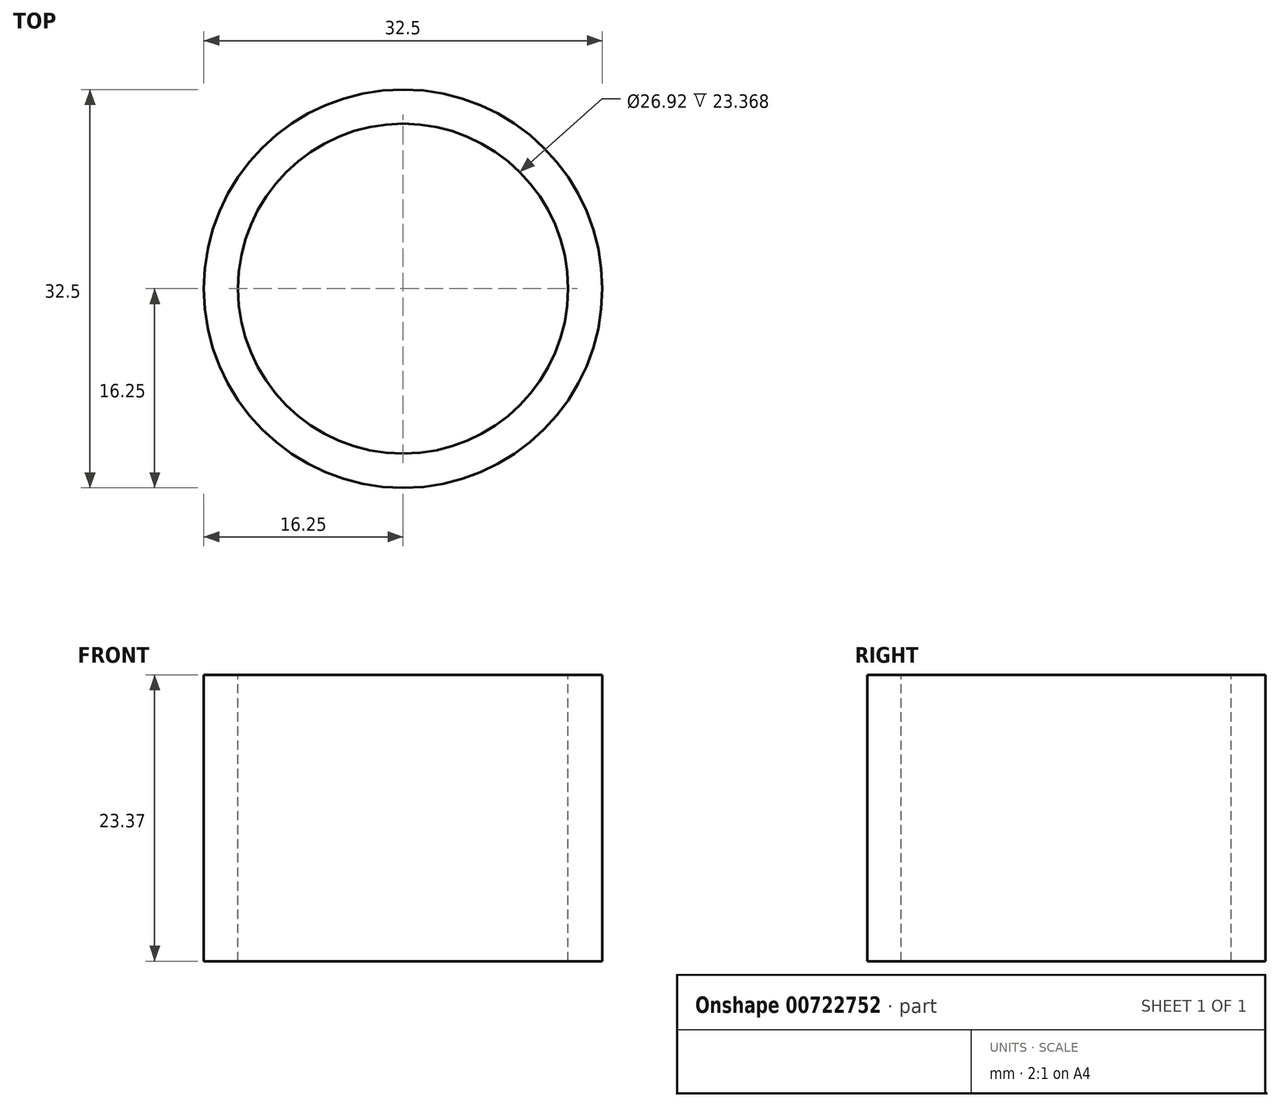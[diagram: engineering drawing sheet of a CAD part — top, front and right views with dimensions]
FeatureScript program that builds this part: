
annotation { "Feature Type Name" : "Feature", "Feature Type Description" : "" }
export const myFeature = defineFeature(function(context is Context, id is Id, definition is map)
    precondition{}
    {
        {
            var Q0;
            Q0=qCreatedBy(makeId("Top.planeOp"),FACE);
            var sketch = newSketch(context, id + "F0", { "sketchPlane" : qUnion([Q0])});
            skCircle(sketch, "E0", {"center": v(0, 0) * mm, "radius": 16.25 * mm});
            skSolve(sketch);
        }
        {
            var Q0;
            Q0=makeQuery(id+"F0.imprint","IMPRINT",FACE,{"disambiguationData":[TD([[makeQuery(id+"F0.imprint","IMPRINT",EDGE,{"derivedFrom":sQuery(id+"F0.wireOp",EDGE,"E0")}),1.0]])]});
            extrude(context, id + "F1", {"entities" : qUnion([Q0]), "depth" : 23.37 * mm, "offsetDistance" : 25.4 * mm});
        }
        {
            var Q0;
            Q0=makeQuery(id+"F1.opExtrude","CAP_FACE",FACE,{"disambiguationData":[OSD([sQuery(id+"F0.wireOp",EDGE,"E0")])],"isStart":false});
            var sketch = newSketch(context, id + "F2", { "sketchPlane" : qUnion([Q0])});
            skPoint(sketch, "E1", {"position": v(0, 0) * mm});
            skSolve(sketch);
        }
        {
            var Q0;
            Q0=makeQuery(id+"F2.imprint","IMPRINT",FACE,{"disambiguationData":[TD([[makeQuery(id+"F2.imprint","IMPRINT",EDGE,{"derivedFrom":makeQuery(id+"F1.opExtrude","CAP_EDGE",EDGE,{"disambiguationData":[OSD([sQuery(id+"F0.wireOp",EDGE,"E0")])],"isStart":false})}),1.0]])]});
            var sketch = newSketch(context, id + "F3", { "sketchPlane" : qUnion([Q0])});
            skPoint(sketch, "E2", {"position": v(0, 0) * mm});
            skSolve(sketch);
        }
        {
            var Q0;
            Q0=sQuery(id+"F3.wireOp",VERTEX,"E2");
            var Q1;
            Q1=makeQuery(id+"F1.opExtrude","SWEPT_BODY",BODY,{"disambiguationData":[OSD([sQuery(id+"F0.wireOp",EDGE,"E0")])]});
            hole(context, id + "F4", {"style" : HoleStyle.SIMPLE, "endStyle" : HoleEndStyle.BLIND, "holeDiameter" : 26.92 * mm, "majorDiameter" : 6.35 * mm, "holeDepth" : 127 * mm, "isTappedThrough" : true, "tappedDepth" : 12.7 * mm, "tapClearance" : 3, "startFromSketch" : true, "locations" : qUnion([Q0]), "scope" : qUnion([Q1])});
        }
    });
